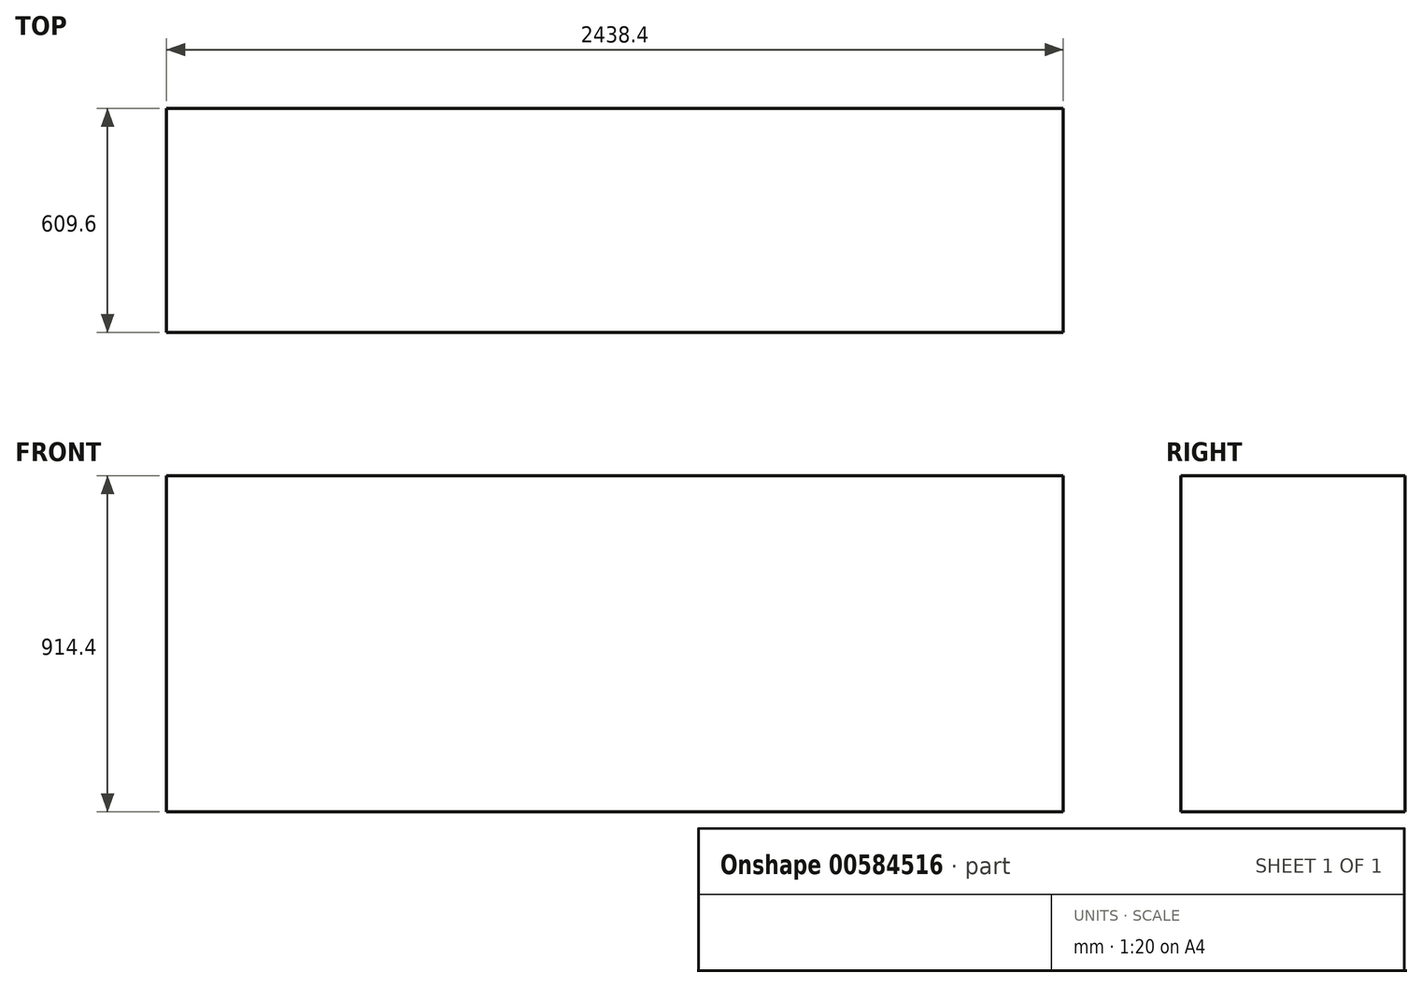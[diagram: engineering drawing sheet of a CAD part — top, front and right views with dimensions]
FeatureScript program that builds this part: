
annotation { "Feature Type Name" : "Feature", "Feature Type Description" : "" }
export const myFeature = defineFeature(function(context is Context, id is Id, definition is map)
    precondition{}
    {
        {
            var Q0;
            Q0=qCreatedBy(makeId("Top.planeOp"),FACE);
            var sketch = newSketch(context, id + "F0", { "sketchPlane" : qUnion([Q0])});
            skLineSegment(sketch, "E0.bottom", {"start": v(0, 0) * mm, "end": v(2438.4, 0) * mm});
            skLineSegment(sketch, "E0.top", {"start": v(0, -609.6) * mm, "end": v(2438.4, -609.6) * mm});
            skLineSegment(sketch, "E0.left", {"start": v(0, 0) * mm, "end": v(0, -609.6) * mm});
            skLineSegment(sketch, "E0.right", {"start": v(2438.4, 0) * mm, "end": v(2438.4, -609.6) * mm});
            skSolve(sketch);
        }
        {
            var Q0;
            Q0 = qSketchRegion(id + "F0", true);
            extrude(context, id + "F1", {"entities" : qUnion([Q0]), "depth" : 914.4 * mm, "offsetDistance" : 25.4 * mm});
        }
    });
